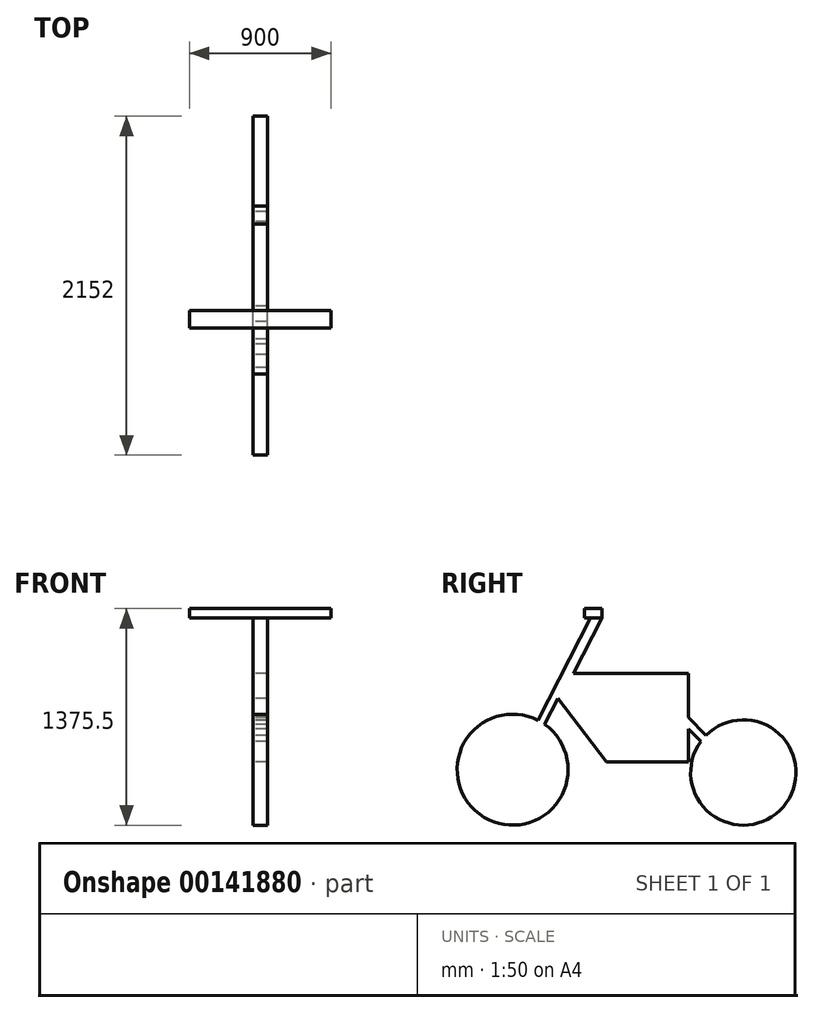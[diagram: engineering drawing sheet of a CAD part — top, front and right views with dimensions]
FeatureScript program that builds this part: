
annotation { "Feature Type Name" : "Feature", "Feature Type Description" : "" }
export const myFeature = defineFeature(function(context is Context, id is Id, definition is map)
    precondition{}
    {
        {
            var Q0;
            Q0=qCreatedBy(makeId("Right.planeOp"),FACE);
            var sketch = newSketch(context, id + "F0", { "sketchPlane" : qUnion([Q0])});
            skCircle(sketch, "E0", {"center": v(0, 0) * mm, "radius": 352.5 * mm});
            skLineSegment(sketch, "E1", {"start": v(0, 0) * mm, "end": v(511, 993) * mm});
            skCircle(sketch, "E2", {"center": v(1465, -18) * mm, "radius": 334.5 * mm});
            skLineSegment(sketch, "E3", {"start": v(0, -352.5) * mm, "end": v(1465, -352.5) * mm, "construction": true});
            skLineSegment(sketch, "E4", {"start": v(1465, -18) * mm, "end": v(1465, -352.5) * mm, "construction": true});
            skLineSegment(sketch, "E5", {"start": v(315.2, 612.5) * mm, "end": v(1115.2, 612.5) * mm});
            skLineSegment(sketch, "E6", {"start": v(595.2, 48.34) * mm, "end": v(1115.2, 48.34) * mm});
            skLineSegment(sketch, "E7", {"start": v(595.2, 48.34) * mm, "end": v(255.5, 496.5) * mm});
            skLineSegment(sketch, "E8", {"start": v(1115.2, 48.34) * mm, "end": v(1115.2, 612.5) * mm});
            skLineSegment(sketch, "E9", {"start": v(1115.2, 330.42) * mm, "end": v(1465, -18) * mm});
            skPoint(sketch, "E10", {"position": v(-352.5, -352.5) * mm});
            skLineSegment(sketch, "E11", {"start": v(-352.5, -352.5) * mm, "end": v(-352.5, 0) * mm, "construction": true});
            skLineSegment(sketch, "E12.bottom", {"start": v(566, 963) * mm, "end": v(456, 963) * mm});
            skLineSegment(sketch, "E12.top", {"start": v(566, 1023) * mm, "end": v(456, 1023) * mm});
            skLineSegment(sketch, "E12.left", {"start": v(566, 963) * mm, "end": v(566, 1023) * mm});
            skLineSegment(sketch, "E12.right", {"start": v(456, 963) * mm, "end": v(456, 1023) * mm});
            skPoint(sketch, "E12.middle", {"position": v(511, 993) * mm});
            skLineSegment(sketch, "E13", {"start": v(566, 963) * mm, "end": v(385.63, 612.5) * mm});
            skLineSegment(sketch, "E14", {"start": v(287.65, 454.08) * mm, "end": v(202.47, 288.55) * mm});
            skLineSegment(sketch, "E15", {"start": v(1115.2, 259.85) * mm, "end": v(1195.38, 179.98) * mm});
            skSolve(sketch);
        }
        {
            var Q0;
            {var subQ0=sQuery(id+"F0.wireOp",EDGE,"E1");var subQ1=sQuery(id+"F0.wireOp",EDGE,"E0");var subQ2=makeQuery(id+"F0.imprint","INTERSECT",VERTEX,{"derivedFrom":[subQ1,subQ0]});Q0=makeQuery(id+"F0.imprint","IMPRINT",FACE,{"disambiguationData":[TD([[makeQuery(id+"F0.imprint","IMPRINT",EDGE,{"disambiguationData":[TD([[subQ2,-1.0]])],"derivedFrom":subQ1}),1.0]])]});}
            var Q1;
            {var subQ0=sQuery(id+"F0.wireOp",EDGE,"E1");var subQ1=sQuery(id+"F0.wireOp",EDGE,"E0");var subQ2=makeQuery(id+"F0.imprint","INTERSECT",VERTEX,{"derivedFrom":[subQ1,subQ0]});Q1=makeQuery(id+"F0.imprint","IMPRINT",FACE,{"disambiguationData":[TD([[makeQuery(id+"F0.imprint","IMPRINT",EDGE,{"disambiguationData":[TD([[subQ2,1.0]])],"derivedFrom":subQ1}),1.0]])]});}
            var Q2;
            {var subQ0=sQuery(id+"F0.wireOp",EDGE,"E1");var subQ1=sQuery(id+"F0.wireOp",EDGE,"E0");var subQ2=makeQuery(id+"F0.imprint","INTERSECT",VERTEX,{"derivedFrom":[subQ1,subQ0]});Q2=makeQuery(id+"F0.imprint","IMPRINT",FACE,{"disambiguationData":[TD([[makeQuery(id+"F0.imprint","IMPRINT",EDGE,{"disambiguationData":[TD([[subQ2,1.0]])],"derivedFrom":subQ1}),-1.0]])]});}
            var Q3;
            {var subQ1=sQuery(id+"F0.wireOp",EDGE,"E5");Q3=makeQuery(id+"F0.imprint","IMPRINT",FACE,{"disambiguationData":[TD([[makeQuery(id+"F0.imprint","IMPRINT",EDGE,{"derivedFrom":subQ1}),-1.0]])]});}
            var Q4;
            {var subQ0=sQuery(id+"F0.wireOp",EDGE,"jfq9GMJ6-YykM-ejGt-zega-1jMZzC7pa4MC");var subQ1=sQuery(id+"F0.wireOp",EDGE,"E2");var subQ2=makeQuery(id+"F0.imprint","INTERSECT",VERTEX,{"derivedFrom":[subQ1,subQ0]});Q4=makeQuery(id+"F0.imprint","IMPRINT",FACE,{"disambiguationData":[TD([[makeQuery(id+"F0.imprint","IMPRINT",EDGE,{"disambiguationData":[TD([[subQ2,1.0]])],"derivedFrom":subQ1}),-1.0]])]});}
            var Q5;
            {var subQ0=sQuery(id+"F0.wireOp",EDGE,"jfq9GMJ6-YykM-ejGt-zega-1jMZzC7pa4MC");var subQ1=sQuery(id+"F0.wireOp",EDGE,"E2");var subQ2=makeQuery(id+"F0.imprint","INTERSECT",VERTEX,{"derivedFrom":[subQ1,subQ0]});Q5=makeQuery(id+"F0.imprint","IMPRINT",FACE,{"disambiguationData":[TD([[makeQuery(id+"F0.imprint","IMPRINT",EDGE,{"disambiguationData":[TD([[subQ2,-1.0]])],"derivedFrom":subQ1}),1.0]])]});}
            var Q6;
            {var subQ0=sQuery(id+"F0.wireOp",EDGE,"jfq9GMJ6-YykM-ejGt-zega-1jMZzC7pa4MC");var subQ1=sQuery(id+"F0.wireOp",EDGE,"E2");var subQ2=makeQuery(id+"F0.imprint","INTERSECT",VERTEX,{"derivedFrom":[subQ1,subQ0]});Q6=makeQuery(id+"F0.imprint","IMPRINT",FACE,{"disambiguationData":[TD([[makeQuery(id+"F0.imprint","IMPRINT",EDGE,{"disambiguationData":[TD([[subQ2,1.0]])],"derivedFrom":subQ1}),1.0]])]});}
            var Q7;
            {var subQ5=sQuery(id+"F0.wireOp",EDGE,"E13");Q7=makeQuery(id+"F0.imprint","IMPRINT",FACE,{"disambiguationData":[TD([[makeQuery(id+"F0.imprint","IMPRINT",EDGE,{"derivedFrom":subQ5}),-1.0]])]});}
            var Q8;
            Q8=makeQuery(id+"F0.imprint","IMPRINT",FACE,{"disambiguationData":[TD([[makeQuery(id+"F0.imprint","IMPRINT",EDGE,{"derivedFrom":sQuery(id+"F0.wireOp",EDGE,"E12.top")}),1.0]])]});
            extrude(context, id + "F1", {"entities" : qUnion([Q0, Q1, Q2, Q3, Q4, Q5, Q6, Q7, Q8]), "depth" : 90 * mm, "symmetric" : true});
        }
        {
            var Q0;
            Q0=makeQuery(id+"F0.imprint","IMPRINT",FACE,{"disambiguationData":[TD([[makeQuery(id+"F0.imprint","IMPRINT",EDGE,{"derivedFrom":sQuery(id+"F0.wireOp",EDGE,"E12.top")}),1.0]])]});
            extrude(context, id + "F2", {"entities" : qUnion([Q0]), "operationType" : NewBodyOperationType.ADD, "depth" : 900 * mm, "symmetric" : true});
        }
    });
